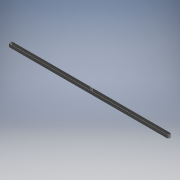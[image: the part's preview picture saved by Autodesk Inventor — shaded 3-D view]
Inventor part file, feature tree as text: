
AUTODESK INVENTOR PART (.ipt)
format: ipt  version: 2017.3 (Build 213256000, 256)  size: 146,944 bytes
history: native  units: mm (DEFAULTED — no unit token found)
features: extrude x2
ambient origin geometry x8: Origin, YZ Plane, XZ Plane, XY Plane, X Axis, Y Axis, Z Axis, Center Point
bodies: Solid1 (feature_tree)
feature tree (2):
  extrude  "Extrusion1"  Depth=15.0mm TaperAngle=0.0deg
  extrude  "Extrusion2"  Depth=15.0mm TaperAngle=0.0deg
